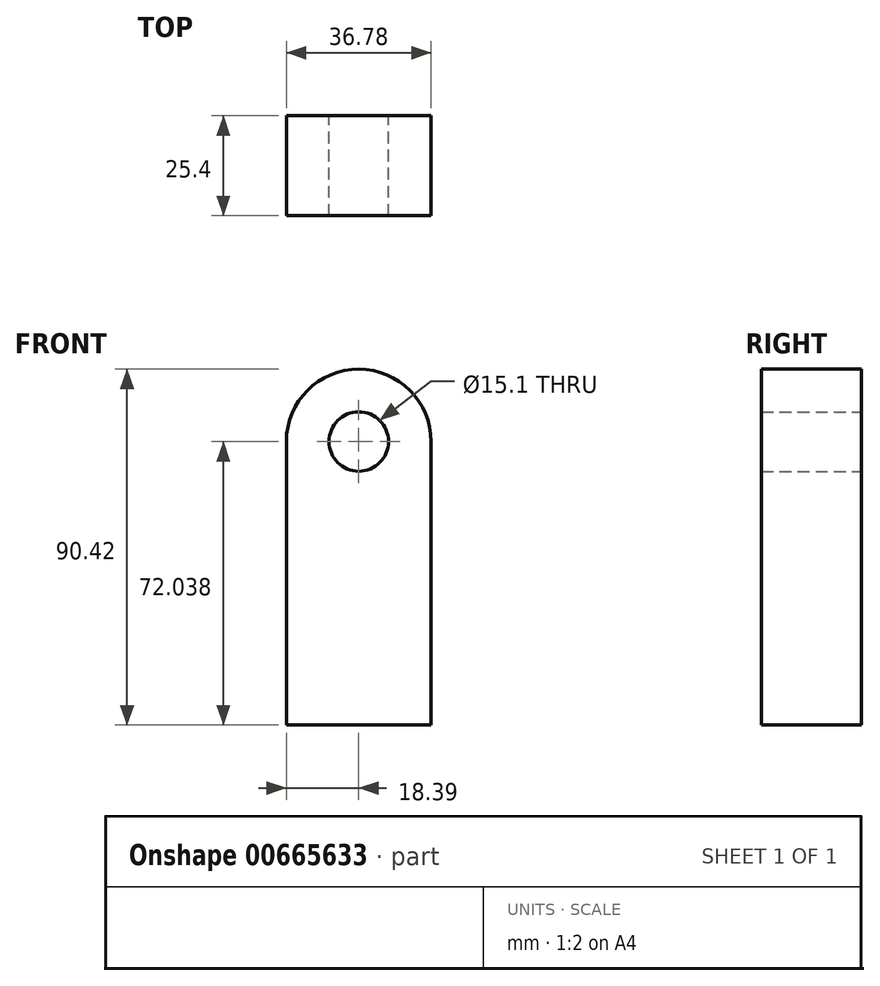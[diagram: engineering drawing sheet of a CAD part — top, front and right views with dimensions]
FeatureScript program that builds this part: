
annotation { "Feature Type Name" : "Feature", "Feature Type Description" : "" }
export const myFeature = defineFeature(function(context is Context, id is Id, definition is map)
    precondition{}
    {
        {
            var Q0;
            Q0=qCreatedBy(makeId("Front.planeOp"),FACE);
            var sketch = newSketch(context, id + "F0", { "sketchPlane" : qUnion([Q0])});
            skLineSegment(sketch, "E0.bottom", {"start": v(18.39, -10.33) * mm, "end": v(-18.39, -10.33) * mm});
            skLineSegment(sketch, "E0.left", {"start": v(18.39, -10.33) * mm, "end": v(18.39, 61.7) * mm});
            skLineSegment(sketch, "E0.right", {"start": v(-18.39, -10.33) * mm, "end": v(-18.39, 61.7) * mm});
            skPoint(sketch, "E0.middle", {"position": v(0, 25.69) * mm});
            skArc(sketch, "E1", {"start": v(18.39, 61.7) * mm, "mid": v(0, 80.1) * mm, "end": v(-18.39, 61.7) * mm});
            skCircle(sketch, "E2", {"center": v(0, 61.7) * mm, "radius": 7.55 * mm});
            skSolve(sketch);
        }
        {
            var Q0;
            Q0=makeQuery(id+"F0.imprint","IMPRINT",FACE,{"disambiguationData":[TD([[makeQuery(id+"F0.imprint","IMPRINT",EDGE,{"derivedFrom":sQuery(id+"F0.wireOp",EDGE,"E0.bottom")}),-1.0]])]});
            extrude(context, id + "F1", {"entities" : qUnion([Q0]), "depth" : 25.4 * mm, "offsetDistance" : 25.4 * mm});
        }
    });
